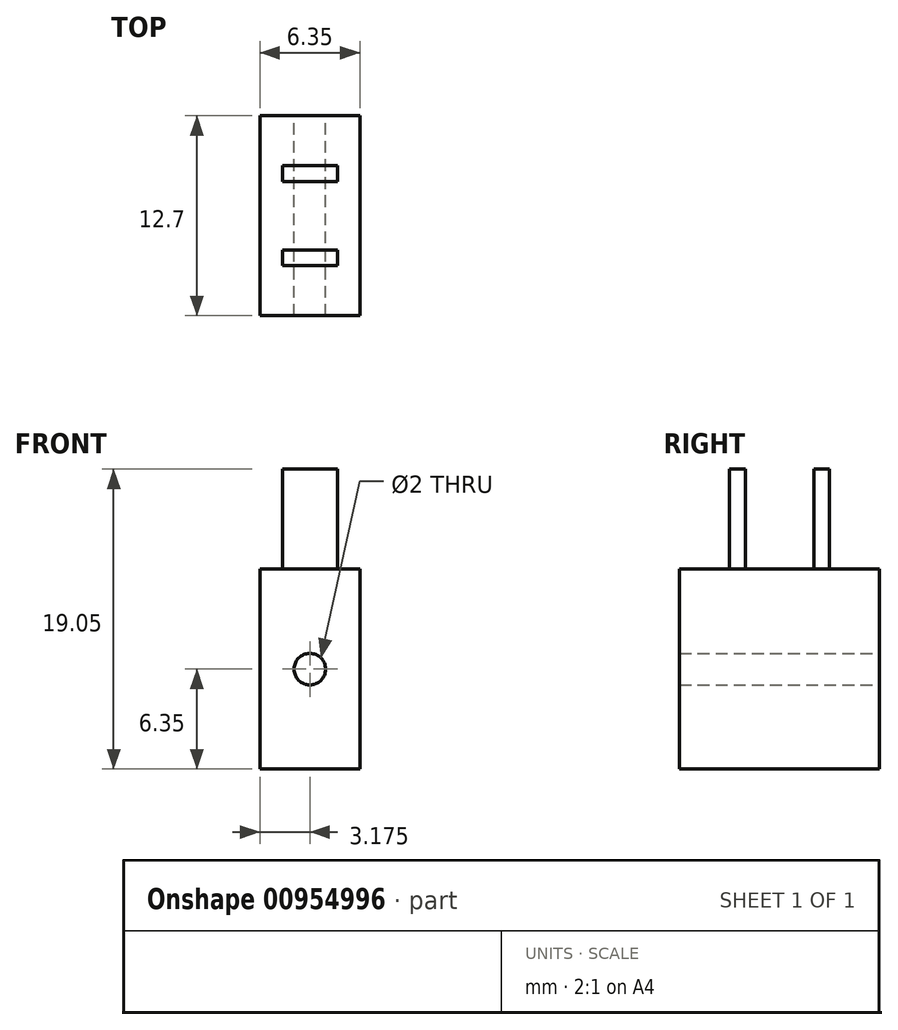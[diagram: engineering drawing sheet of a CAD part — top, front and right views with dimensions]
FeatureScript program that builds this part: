
annotation { "Feature Type Name" : "Feature", "Feature Type Description" : "" }
export const myFeature = defineFeature(function(context is Context, id is Id, definition is map)
    precondition{}
    {
        {
            var Q0;
            Q0=qCreatedBy(makeId("Top.planeOp"),FACE);
            var sketch = newSketch(context, id + "F0", { "sketchPlane" : qUnion([Q0])});
            skLineSegment(sketch, "E0.bottom", {"start": v(0, 0) * mm, "end": v(6.35, 0) * mm});
            skLineSegment(sketch, "E0.top", {"start": v(0, 12.7) * mm, "end": v(6.35, 12.7) * mm});
            skLineSegment(sketch, "E0.left", {"start": v(0, 0) * mm, "end": v(0, 12.7) * mm});
            skLineSegment(sketch, "E0.right", {"start": v(6.35, 0) * mm, "end": v(6.35, 12.7) * mm});
            skSolve(sketch);
        }
        {
            var Q0;
            Q0 = qSketchRegion(id + "F0", true);
            extrude(context, id + "F1", {"entities" : qUnion([Q0]), "depth" : 12.7 * mm, "offsetDistance" : 25.4 * mm});
        }
        {
            var Q0;
            Q0=makeQuery(id+"F1.opExtrude","CAP_FACE",FACE,{"disambiguationData":[OSD([sQuery(id+"F0.wireOp",EDGE,"E0.bottom"),sQuery(id+"F0.wireOp",EDGE,"E0.top"),sQuery(id+"F0.wireOp",EDGE,"E0.left"),sQuery(id+"F0.wireOp",EDGE,"E0.right")])],"isStart":false});
            var sketch = newSketch(context, id + "F2", { "sketchPlane" : qUnion([Q0])});
            skLineSegment(sketch, "E1.bottom", {"start": v(1.42, 9.52) * mm, "end": v(4.92, 9.52) * mm});
            skLineSegment(sketch, "E1.top", {"start": v(1.42, 8.52) * mm, "end": v(4.92, 8.52) * mm});
            skLineSegment(sketch, "E1.left", {"start": v(1.42, 9.52) * mm, "end": v(1.42, 8.52) * mm});
            skLineSegment(sketch, "E1.right", {"start": v(4.92, 9.52) * mm, "end": v(4.92, 8.52) * mm});
            skLineSegment(sketch, "E2.bottom", {"start": v(1.42, 4.17) * mm, "end": v(4.93, 4.17) * mm});
            skLineSegment(sketch, "E2.top", {"start": v(1.42, 3.18) * mm, "end": v(4.93, 3.18) * mm});
            skLineSegment(sketch, "E2.left", {"start": v(1.42, 4.17) * mm, "end": v(1.42, 3.18) * mm});
            skLineSegment(sketch, "E2.right", {"start": v(4.92, 4.17) * mm, "end": v(4.92, 3.18) * mm});
            skPoint(sketch, "E3", {"position": v(3.17, 12.7) * mm});
            skPoint(sketch, "E4", {"position": v(3.17, 9.52) * mm});
            skPoint(sketch, "E5", {"position": v(3.17, 4.17) * mm});
            skSolve(sketch);
        }
        {
            var Q0;
            Q0 = qSketchRegion(id + "F2", true);
            extrude(context, id + "F3", {"entities" : qUnion([Q0]), "operationType" : NewBodyOperationType.ADD, "depth" : 6.35 * mm, "offsetDistance" : 25.4 * mm});
        }
        {
            var Q0;
            Q0=makeQuery(id+"F1.opExtrude","SWEPT_FACE",FACE,{"disambiguationData":[OSD([sQuery(id+"F0.wireOp",EDGE,"E0.top")])]});
            var sketch = newSketch(context, id + "F4", { "sketchPlane" : qUnion([Q0])});
            skPoint(sketch, "E6", {"position": v(-6.35, 6.35) * mm});
            skPoint(sketch, "E7", {"position": v(-3.17, 0) * mm});
            skCircle(sketch, "E8", {"center": v(-3.17, 6.35) * mm, "radius": 1 * mm});
            skSolve(sketch);
        }
        {
            var Q0;
            Q0 = qSketchRegion(id + "F4", true);
            extrude(context, id + "F5", {"entities" : qUnion([Q0]), "operationType" : NewBodyOperationType.REMOVE, "endBound" : BoundingType.THROUGH_ALL, "oppositeDirection" : true, "depth" : 25.4 * mm, "offsetDistance" : 25.4 * mm});
        }
    });
